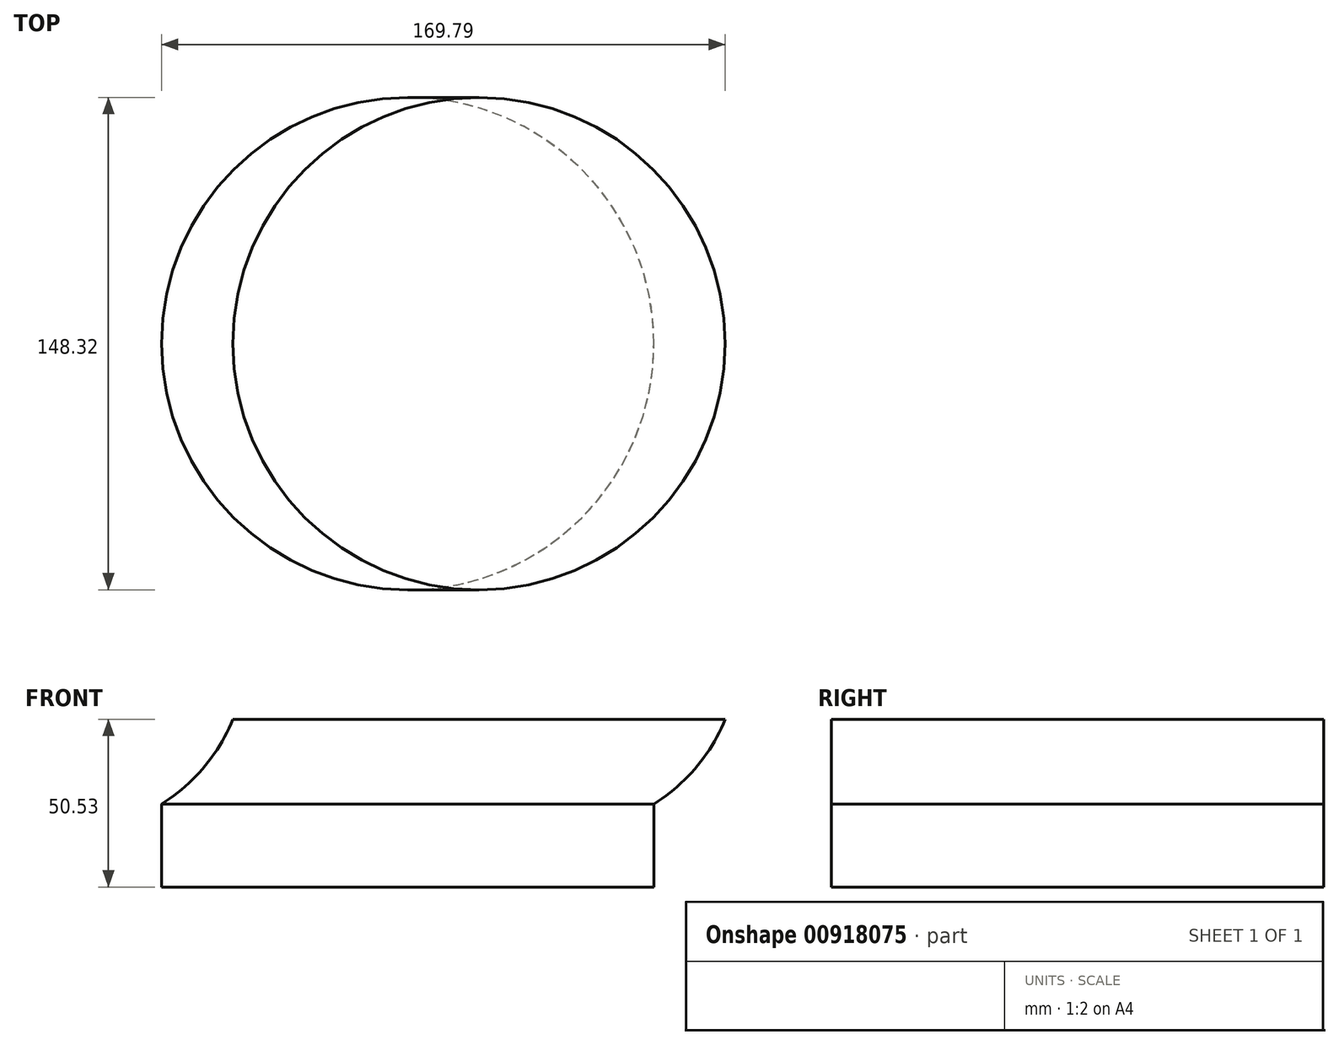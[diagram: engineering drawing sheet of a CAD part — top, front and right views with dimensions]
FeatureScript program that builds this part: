
annotation { "Feature Type Name" : "Feature", "Feature Type Description" : "" }
export const myFeature = defineFeature(function(context is Context, id is Id, definition is map)
    precondition{}
    {
        {
            var Q0;
            Q0=qCreatedBy(makeId("Top.planeOp"),FACE);
            var sketch = newSketch(context, id + "F0", { "sketchPlane" : qUnion([Q0])});
            skCircle(sketch, "E0", {"center": v(-34.1, -5.7) * mm, "radius": 74.16 * mm});
            skSolve(sketch);
        }
        {
            var Q0;
            Q0 = qSketchRegion(id + "F0", true);
            extrude(context, id + "F1", {"entities" : qUnion([Q0]), "depth" : 25 * mm, "offsetDistance" : 25 * mm});
        }
        {
            var Q0;
            Q0=qCreatedBy(makeId("Front.planeOp"),FACE);
            var sketch = newSketch(context, id + "F2", { "sketchPlane" : qUnion([Q0])});
            skArc(sketch, "E1", {"start": v(-21.47, 62) * mm, "mid": v(-8.71, 73.07) * mm, "end": v(0, 87.54) * mm});
            skArc(sketch, "E2", {"start": v(54.08, 147.34) * mm, "mid": v(13.5, 129.68) * mm, "end": v(0, 87.54) * mm});
            skSolve(sketch);
        }
        {
            var Q0;
            Q0=makeQuery(id+"F1.opExtrude","CAP_FACE",FACE,{"disambiguationData":[OSD([sQuery(id+"F0.wireOp",EDGE,"E0")])],"isStart":false});
            var Q1;
            Q1=sQuery(id+"F2.wireOp",EDGE,"E1");
            sweep(context, id + "F3", {"operationType" : NewBodyOperationType.ADD, "profiles" : qUnion([Q0]), "path" : qUnion([Q1]), "keepProfileOrientation" : true});
        }
    });
